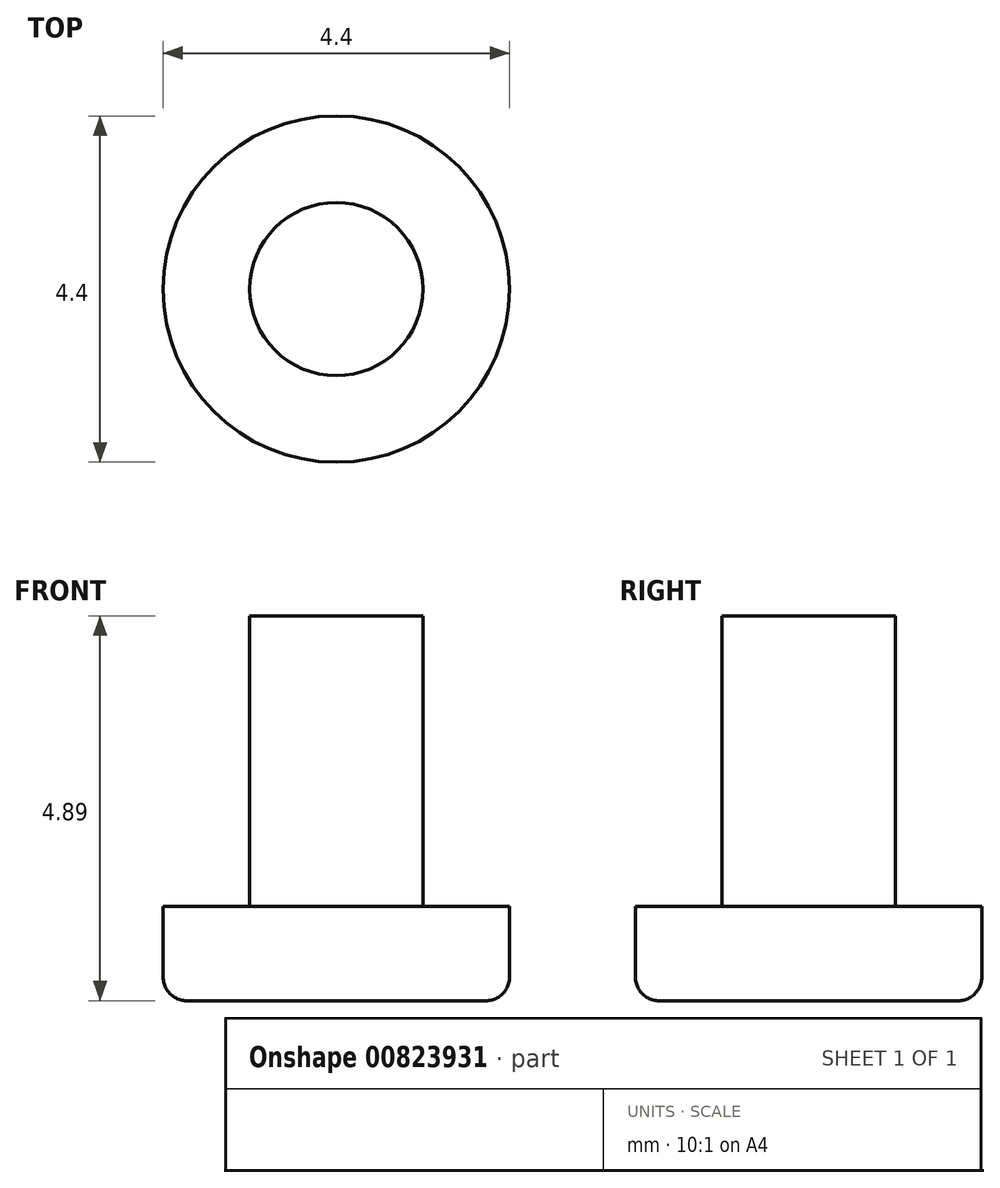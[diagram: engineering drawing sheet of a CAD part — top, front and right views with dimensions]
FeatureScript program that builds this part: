
annotation { "Feature Type Name" : "Feature", "Feature Type Description" : "" }
export const myFeature = defineFeature(function(context is Context, id is Id, definition is map)
    precondition{}
    {
        {
            var Q0;
            Q0=qCreatedBy(makeId("Front.planeOp"),FACE);
            var sketch = newSketch(context, id + "F0", { "sketchPlane" : qUnion([Q0])});
            skLineSegment(sketch, "E0.bottom", {"start": v(0, 0) * mm, "end": v(-1.1, 0) * mm});
            skLineSegment(sketch, "E0.top", {"start": v(0, 3.69) * mm, "end": v(-1.1, 3.69) * mm});
            skLineSegment(sketch, "E0.left", {"start": v(0, 0) * mm, "end": v(0, 3.69) * mm});
            skLineSegment(sketch, "E0.right", {"start": v(-1.1, 0) * mm, "end": v(-1.1, 3.7) * mm});
            skLineSegment(sketch, "E1.bottom", {"start": v(0, 0) * mm, "end": v(-2.2, 0) * mm});
            skLineSegment(sketch, "E1.top", {"start": v(0, -1.2) * mm, "end": v(-2.2, -1.2) * mm});
            skLineSegment(sketch, "E1.left", {"start": v(0, 0) * mm, "end": v(0, -1.2) * mm});
            skLineSegment(sketch, "E1.right", {"start": v(-2.2, 0) * mm, "end": v(-2.2, -1.2) * mm});
            skLineSegment(sketch, "E2.bottom", {"start": v(-2.2, 0) * mm, "end": v(0, 0) * mm});
            skLineSegment(sketch, "E2.top", {"start": v(-2.2, -0.9) * mm, "end": v(0, -0.9) * mm});
            skLineSegment(sketch, "E2.left", {"start": v(-2.2, 0) * mm, "end": v(-2.2, -0.9) * mm});
            skLineSegment(sketch, "E2.right", {"start": v(0, 0) * mm, "end": v(0, -0.9) * mm});
            skLineSegment(sketch, "E3.bottom", {"start": v(0, 0) * mm, "end": v(-1.9, 0) * mm});
            skLineSegment(sketch, "E3.top", {"start": v(0, -1.2) * mm, "end": v(-1.9, -1.2) * mm});
            skLineSegment(sketch, "E3.right", {"start": v(-1.9, 0) * mm, "end": v(-1.9, -1.2) * mm});
            skArc(sketch, "E4", {"start": v(-2.2, -0.9) * mm, "mid": v(-2.11, -1.11) * mm, "end": v(-1.9, -1.2) * mm});
            skSolve(sketch);
        }
        {
            var Q0;
            Q0=makeQuery(id+"F0.imprint","IMPRINT",FACE,{"disambiguationData":[TD([[makeQuery(id+"F0.imprint","IMPRINT",EDGE,{"derivedFrom":sQuery(id+"F0.wireOp",EDGE,"E0.bottom")}),-1.0]])]});
            var Q1;
            {var subQ5=sQuery(id+"F0.wireOp",EDGE,"E0.bottom");Q1=makeQuery(id+"F0.imprint","IMPRINT",FACE,{"disambiguationData":[TD([[makeQuery(id+"F0.imprint","IMPRINT",EDGE,{"derivedFrom":subQ5}),1.0]])]});}
            var Q2;
            {var subQ0=sQuery(id+"F0.wireOp",EDGE,"E1.left");var subQ1=sQuery(id+"F0.wireOp",EDGE,"E1.top");var subQ2=makeQuery(id+"F0.imprint","INTERSECT",VERTEX,{"derivedFrom":[subQ1,subQ0]});Q2=makeQuery(id+"F0.imprint","IMPRINT",FACE,{"disambiguationData":[TD([[makeQuery(id+"F0.imprint","IMPRINT",EDGE,{"disambiguationData":[TD([[subQ2,1.0]])],"derivedFrom":subQ0}),-1.0]])]});}
            var Q3;
            {var subQ3=sQuery(id+"F0.wireOp",EDGE,"E4");Q3=makeQuery(id+"F0.imprint","IMPRINT",FACE,{"disambiguationData":[TD([[makeQuery(id+"F0.imprint","IMPRINT",EDGE,{"derivedFrom":subQ3}),1.0]])]});}
            var Q4;
            {var subQ0=sQuery(id+"F0.wireOp",EDGE,"E1.right");var subQ1=sQuery(id+"F0.wireOp",EDGE,"E1.bottom");var subQ2=makeQuery(id+"F0.imprint","INTERSECT",VERTEX,{"derivedFrom":[subQ1,subQ0]});Q4=makeQuery(id+"F0.imprint","IMPRINT",FACE,{"disambiguationData":[TD([[makeQuery(id+"F0.imprint","IMPRINT",EDGE,{"disambiguationData":[TD([[subQ2,1.0]])],"derivedFrom":subQ1}),1.0]])]});}
            var Q5;
            Q5=sQuery(id+"F0.wireOp",EDGE,"E0.left");
            revolve(context, id + "F1", {"surfaceOperationType" : NewSurfaceOperationType.NEW, "entities" : qUnion([Q0, Q1, Q2, Q3, Q4]), "axis" : qUnion([Q5]), "revolveType" : RevolveType.FULL});
        }
    });
